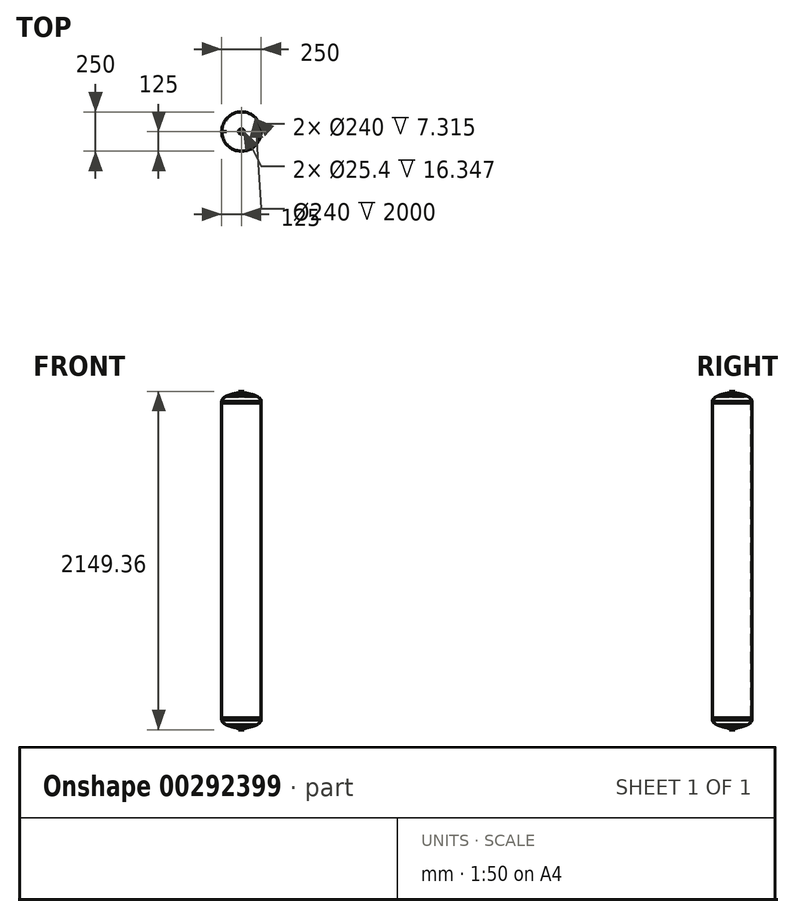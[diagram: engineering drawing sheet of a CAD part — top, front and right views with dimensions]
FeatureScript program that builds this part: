
annotation { "Feature Type Name" : "Feature", "Feature Type Description" : "" }
export const myFeature = defineFeature(function(context is Context, id is Id, definition is map)
    precondition{}
    {
        {
            var Q0;
            Q0=qCreatedBy(makeId("Top.planeOp"),FACE);
            var sketch = newSketch(context, id + "F0", { "sketchPlane" : qUnion([Q0])});
            skCircle(sketch, "E0", {"center": v(0, 0) * mm, "radius": 125 * mm});
            skPoint(sketch, "E1", {"position": v(-125, 0) * mm});
            skPoint(sketch, "E2", {"position": v(125, 0) * mm});
            skSolve(sketch);
        }
        {
            var Q0;
            Q0=qCreatedBy(makeId("Front.planeOp"),FACE);
            var sketch = newSketch(context, id + "F1", { "sketchPlane" : qUnion([Q0])});
            skLineSegment(sketch, "E3", {"start": v(-17.7, 74.68) * mm, "end": v(-17.7, 66.12) * mm});
            skFitSpline(sketch, "E4", {"points": [v(-17.7, 66.12) * mm, v(-94.6, 44.72) * mm, v(-125, 11.34) * mm], "startDerivative": vector(-134.8, -32.11) * mm, "endDerivative": vector(0, -101.43) * mm});
            skLineSegment(sketch, "E5", {"start": v(-125, 0) * mm, "end": v(-125, 11.34) * mm});
            skLineSegment(sketch, "E6", {"start": v(0, -71.97) * mm, "end": v(0, 86.94) * mm, "construction": true});
            skLineSegment(sketch, "E7.2", {"start": v(-12.7, 74.68) * mm, "end": v(-12.7, 58.33) * mm});
            skFitSpline(sketch, "E8", {"points": [v(-12.7, 58.33) * mm, v(-94.6, 39.72) * mm, v(-120, 7.31) * mm], "startDerivative": vector(-139.5, -26.6) * mm, "endDerivative": vector(0, -89.82) * mm});
            skLineSegment(sketch, "E9", {"start": v(-120, 7.31) * mm, "end": v(-120, 0) * mm});
            skLineSegment(sketch, "E10", {"start": v(-120, 0) * mm, "end": v(-125, 0) * mm});
            skLineSegment(sketch, "E11", {"start": v(-17.7, 74.68) * mm, "end": v(-12.7, 74.68) * mm});
            skLineSegment(sketch, "E12", {"start": v(-94.6, 44.72) * mm, "end": v(-94.6, 39.72) * mm});
            skSolve(sketch);
        }
        {
            var Q0;
            Q0=qSketchRegion(id+"F1",true);
            var Q1;
            Q1=sQuery(id+"F1.wireOp",EDGE,"E6");
            revolve(context, id + "F2", {"entities" : qUnion([Q0]), "axis" : qUnion([Q1]), "revolveType" : RevolveType.FULL});
        }
        {
            var Q0;
            Q0=makeQuery(id+"F2.opRevolve","SWEPT_FACE",FACE,{"disambiguationData":[OSD([sQuery(id+"F1.wireOp",EDGE,"E10")])]});
            extrude(context, id + "F3", {"entities" : qUnion([Q0]), "depth" : 2000 * mm});
        }
        {
            var Q0;
            Q0=qCreatedBy(makeId("Top.planeOp"),FACE);
            cPlane(context, id + "F4", {"entities" : qUnion([Q0]), "cplaneType" : CPlaneType.OFFSET, "offset" : 1000 * mm, "oppositeDirection" : true, "width" : 150 * mm, "height" : 150 * mm});
        }
        {
            var Q0;
            Q0=makeQuery(id+"F2.opRevolve","SWEPT_BODY",BODY,{"disambiguationData":[OSD([sQuery(id+"F1.wireOp",EDGE,"E3"),sQuery(id+"F1.wireOp",EDGE,"E4"),sQuery(id+"F1.wireOp",EDGE,"E5"),sQuery(id+"F1.wireOp",EDGE,"E7.2"),sQuery(id+"F1.wireOp",EDGE,"E8"),sQuery(id+"F1.wireOp",EDGE,"E9"),sQuery(id+"F1.wireOp",EDGE,"E10"),sQuery(id+"F1.wireOp",EDGE,"E11")])]});
            var Q1;
            Q1=qCreatedBy(id+"F4.planeOp",FACE);
            mirror(context, id + "F5", {"entities" : qUnion([Q0]), "mirrorPlane" : qUnion([Q1])});
        }
    });
